# Revit family: 71600XXX_new
name_source: partatom
category: Plumbing Fixtures
revit_build: Autodesk Revit 2018 (Build: 20170223_1515(x64)
units: mm (PartAtom-declared; Revit-internal decimal feet)

## family parameters
Always vertical = No
Cut with Voids When Loaded = No
OmniClass Number = 23.31.11.00
OmniClass Title = Faucets
Part Type = Normal
Room Calculation Point = No
Round Connector Dimension = Use Diameter
Shared = No
Work Plane-Based = Yes

## types (1)
- 670 Matte Black
    Always visible = Yes
    BIMobject category = Taps & Mixers
    Connector Description = Water Inlet 12.7mm
    Default Elevation = 1219.2 mm  [stored 4 ft]
    Description = Logis Single lever shower mixer for exposed installation
    Design country = Germany
    Diameter = 13 mm
    Edition number = 1
    IFC Classification = Valve
    Manufacturer = Hansgrohe
    Manufacturer country = Germany
    Manufacturer name = hansgrohe
    Masterformat 2014 Code = 22 41 39
    Masterformat 2014 Description = Residential Faucets, Supplies, and Trim
    Material 1 = Hansgrohe - Metal - 670 Matte Black
    Model = 71600XXX
    OmniClass Code = 23-31 11 00
    OmniClass Description = Faucets
    Product Guid = 43dd4556-5223-4145-803a-bab068d10f3c
    Product SKU = 71600XXX
    Product data url = https://bimobject.com
    Product name = 71600XXX Logis Single lever shower mixer for exposed installation
    Product url = https://www.hansgrohe.com
    QR code = https://bimobject.com
    UNSPSC Code = 301815
    URL = https://www.hansgrohe.com
    Uniclass 2015 Code = Pr_40_20_87
    Uniclass 2015 Name = Taps and water supply outlet fittings
    Uniformat II Code = D2010
    Uniformat II Description = Plumbing Fixtures
    Weight Net (Kg) = 1.6

note: [stored X ft] marks values corroborated as IEEE doubles in the binary element streams (Revit-internal decimal feet)

## geometry (parser evidence)
native form markers: Sweep x1
no freeform markers — native parametric forms only
